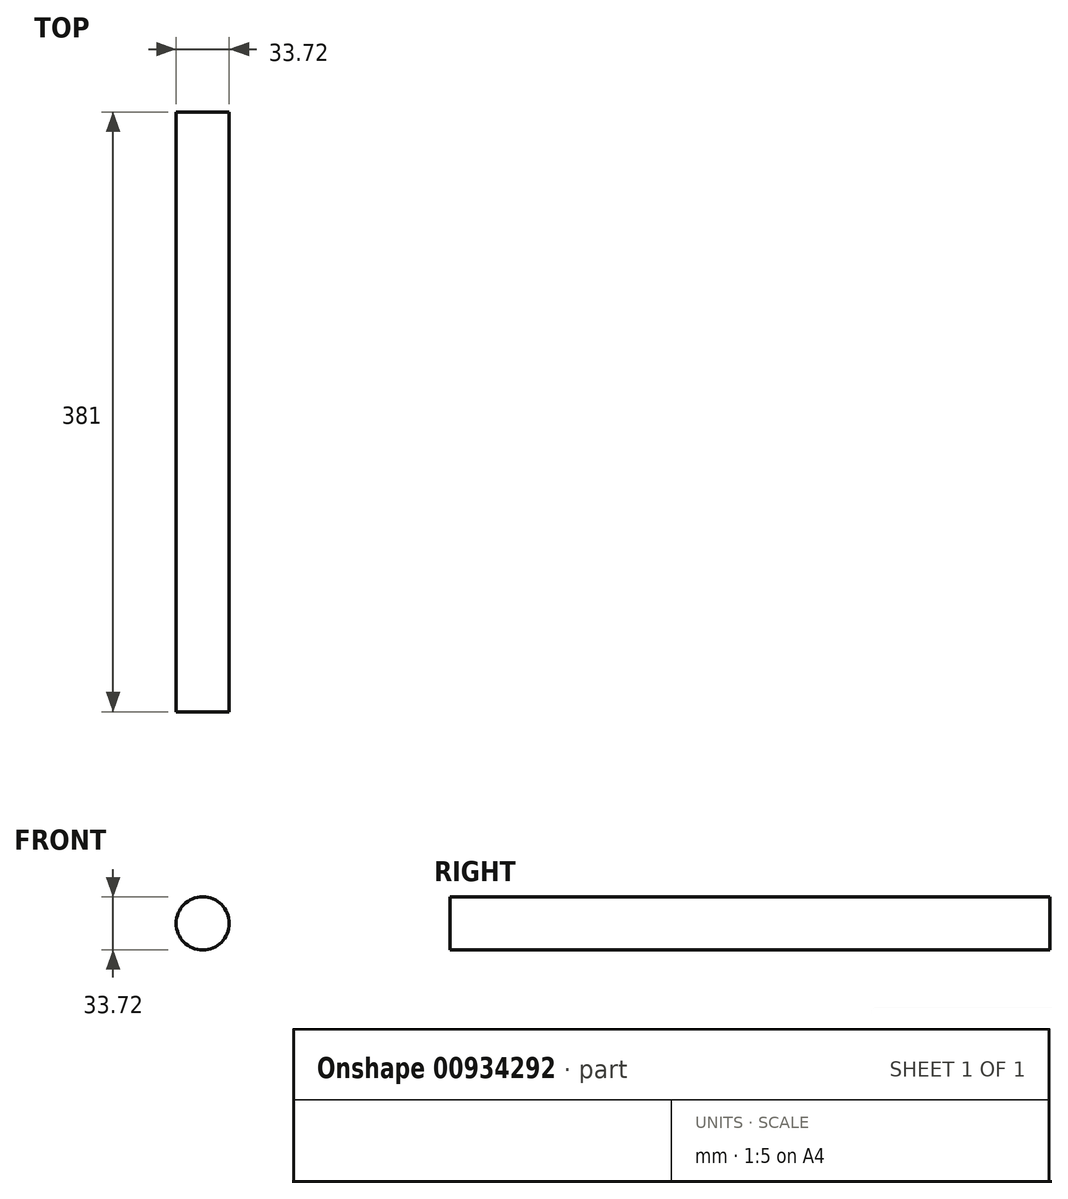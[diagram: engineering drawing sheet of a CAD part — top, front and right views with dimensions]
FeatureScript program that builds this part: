
annotation { "Feature Type Name" : "Feature", "Feature Type Description" : "" }
export const myFeature = defineFeature(function(context is Context, id is Id, definition is map)
    precondition{}
    {
        {
            var Q0;
            Q0=qCreatedBy(makeId("Front.planeOp"),FACE);
            var sketch = newSketch(context, id + "F0", { "sketchPlane" : qUnion([Q0])});
            skCircle(sketch, "E0", {"center": v(0, 0) * mm, "radius": 16.86 * mm});
            skSolve(sketch);
        }
        {
            var Q0;
            Q0=makeQuery(id+"F0.imprint","IMPRINT",FACE,{"disambiguationData":[TD([[makeQuery(id+"F0.imprint","IMPRINT",EDGE,{"derivedFrom":sQuery(id+"F0.wireOp",EDGE,"E0")}),1.0]])]});
            extrude(context, id + "F1", {"entities" : qUnion([Q0]), "depth" : 381 * mm, "offsetDistance" : 25.4 * mm});
        }
    });
